# Revit family: Plum Fix_Tap_Argent_Echo Kitchen Mixer
name_source: partatom
category: Plumbing Fixtures
revit_build: Autodesk Revit 2016 (Build: 20150220_1215(x64)
units: mm (PartAtom-declared; Revit-internal decimal feet)

## family parameters
Always vertical = Yes
Cut with Voids When Loaded = Yes
OmniClass Number = 23.45.55.17
OmniClass Title = Mixing Faucets
Part Type = Normal
Room Calculation Point = No
Round Connector Dimension = Use Diameter
Shared = No
Work Plane-Based = No

## types (1)
- Chrome
    Body Material = z_Argent_Chrome
    CW Connection = Yes
    CWFU = 0
    Cost = 0 $
    Description = Echo Kitchen Mixer WELS 4 Star / 7.5Lpm
    HW Connection = Yes
    HWFU = 0
    Manufacturer = Argent
    Manufacturer_Overall Depth = 266.36 mm
    Manufacturer_Overall Height = 163 mm
    Manufacturer_Overall Width = 45 mm  [stored 0.147638 ft]
    Manufacturer_Spec Code = KM422621
    Manufacturer_URL__Product Specific = https://www.argentaust.com.au
    Model = KM422621
    ModifiedIssue_ANZRS = 20190503 $
    Type Comments = Chrome finish
    URL = https://www.argentaust.com.au
    Vent Connection = No
    WFU = 0
    Waste Connection = No

note: [stored X ft] marks values corroborated as IEEE doubles in the binary element streams (Revit-internal decimal feet)

## geometry (parser evidence)
native form markers: Sweep x2
no freeform markers — native parametric forms only
